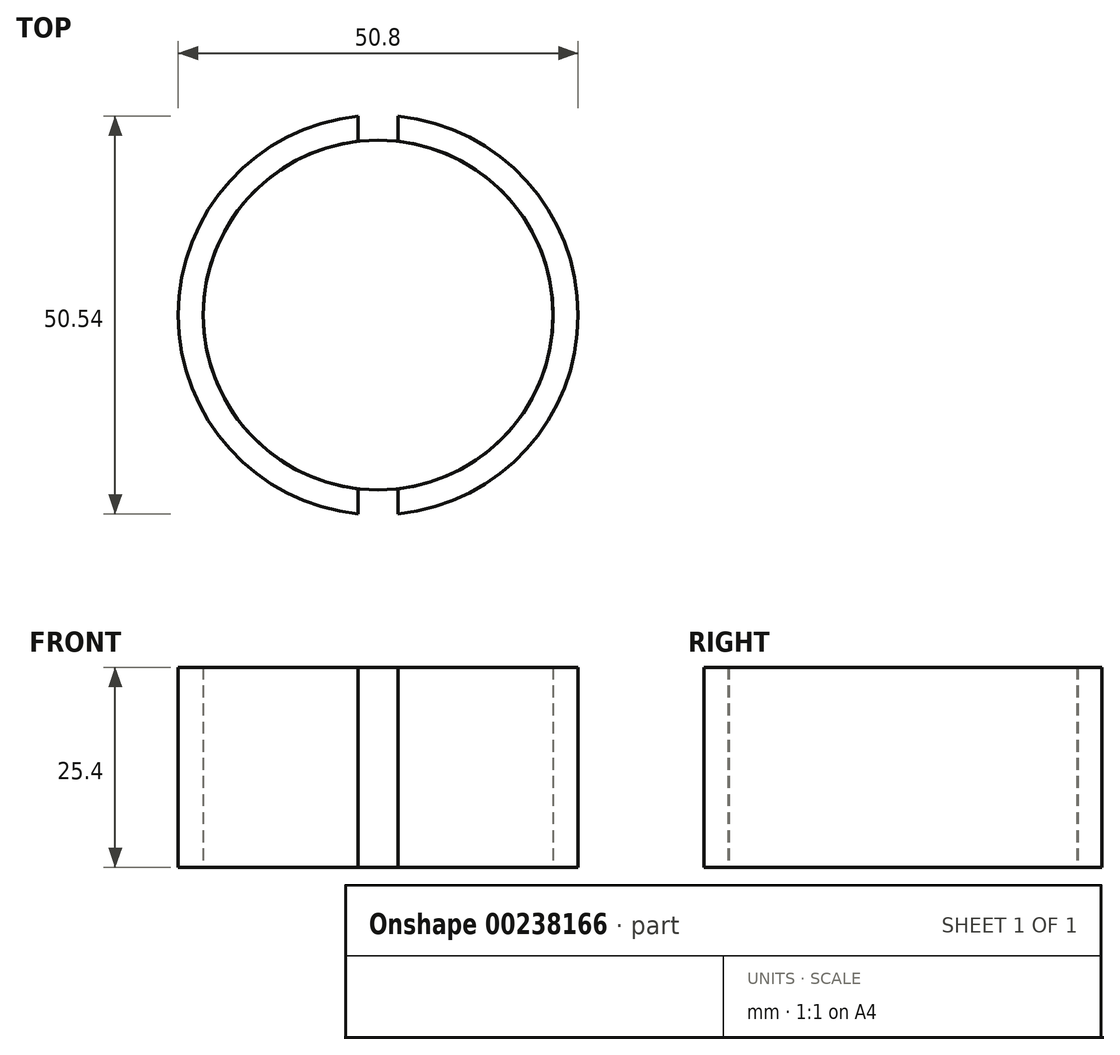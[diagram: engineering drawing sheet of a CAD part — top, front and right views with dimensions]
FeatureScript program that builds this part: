
annotation { "Feature Type Name" : "Feature", "Feature Type Description" : "" }
export const myFeature = defineFeature(function(context is Context, id is Id, definition is map)
    precondition{}
    {
        {
            var Q0;
            Q0=qCreatedBy(makeId("Top.planeOp"),FACE);
            var sketch = newSketch(context, id + "F0", { "sketchPlane" : qUnion([Q0])});
            skCircle(sketch, "E0", {"center": v(0, 0) * mm, "radius": 25.4 * mm});
            skCircle(sketch, "E1", {"center": v(0, 0) * mm, "radius": 22.23 * mm});
            skPoint(sketch, "E2", {"position": v(0, 22.23) * mm});
            skPoint(sketch, "E3", {"position": v(0, 25.4) * mm});
            skPoint(sketch, "E4", {"position": v(0, -22.23) * mm});
            skPoint(sketch, "E5", {"position": v(0, -25.4) * mm});
            skPoint(sketch, "E6", {"position": v(2.54, -22.08) * mm});
            skPoint(sketch, "E7.MirrorP", {"position": v(-2.54, -22.08) * mm});
            skPoint(sketch, "E8", {"position": v(2.54, 25.27) * mm});
            skPoint(sketch, "E9.MirrorP", {"position": v(-2.54, 25.27) * mm});
            skPoint(sketch, "E10", {"position": v(-2.54, -25.27) * mm});
            skPoint(sketch, "E11", {"position": v(2.54, -25.27) * mm});
            skPoint(sketch, "E12", {"position": v(-2.54, 22.08) * mm});
            skPoint(sketch, "E13", {"position": v(2.54, 22.08) * mm});
            skLineSegment(sketch, "E14", {"start": v(-2.54, 25.27) * mm, "end": v(-2.54, 22.08) * mm});
            skLineSegment(sketch, "E15", {"start": v(2.54, 25.27) * mm, "end": v(2.54, 22.08) * mm});
            skLineSegment(sketch, "E16", {"start": v(-2.54, -22.08) * mm, "end": v(-2.54, -25.27) * mm});
            skLineSegment(sketch, "E17", {"start": v(2.54, -22.08) * mm, "end": v(2.54, -25.27) * mm});
            skSolve(sketch);
        }
        {
            var Q0;
            {var subQ0=sQuery(id+"F0.wireOp",EDGE,"E14");Q0=makeQuery(id+"F0.imprint","IMPRINT",FACE,{"disambiguationData":[TD([[makeQuery(id+"F0.imprint","IMPRINT",EDGE,{"derivedFrom":subQ0}),-1.0]])]});}
            var Q1;
            {var subQ0=sQuery(id+"F0.wireOp",EDGE,"E15");Q1=makeQuery(id+"F0.imprint","IMPRINT",FACE,{"disambiguationData":[TD([[makeQuery(id+"F0.imprint","IMPRINT",EDGE,{"derivedFrom":subQ0}),1.0]])]});}
            extrude(context, id + "F1", {"entities" : qUnion([Q0, Q1]), "depth" : 25.4 * mm});
        }
        {
            var Q0;
            Q0=qCreatedBy(makeId("Top.planeOp"),FACE);
            var sketch = newSketch(context, id + "F2", { "sketchPlane" : qUnion([Q0])});
            skCircle(sketch, "E18", {"center": v(0, 0) * mm, "radius": 22.23 * mm});
            skSolve(sketch);
        }
        {
            var Q0;
            Q0=makeQuery(id+"F2.imprint","IMPRINT",FACE,{"disambiguationData":[TD([[makeQuery(id+"F2.imprint","IMPRINT",EDGE,{"derivedFrom":sQuery(id+"F2.wireOp",EDGE,"E18")}),1.0]])]});
            extrude(context, id + "F3", {"entities" : qUnion([Q0]), "depth" : 25.4 * mm});
        }
    });
